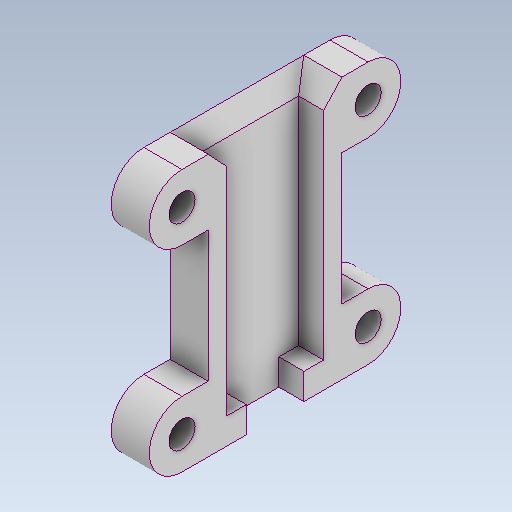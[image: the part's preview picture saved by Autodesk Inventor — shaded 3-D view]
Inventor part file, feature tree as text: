
AUTODESK INVENTOR PART (.ipt)
format: ipt  version: 2020 (Build 240168000, 168)  size: 172,544 bytes
history: native  units: in
note: dims shown in document units (in); Inventor stores cm internally (conversion verified against a paired STEP export)
features: other x3, sketch x3
ambient origin geometry x8: Origin, YZ Plane, XZ Plane, XY Plane, X Axis, Y Axis, Z Axis, Center Point
bodies: Solid1 (feature_tree)
feature tree (6):
  other  "PistonCasingTop.ipt"
  other  "Solid1::PistonCasingTop.ipt"
  other  "TaggingFeature1"
  sketch  "Sketch1"  dims[d0=0.3937in]
  sketch  "Sketch2"
  sketch  "Sketch3"
